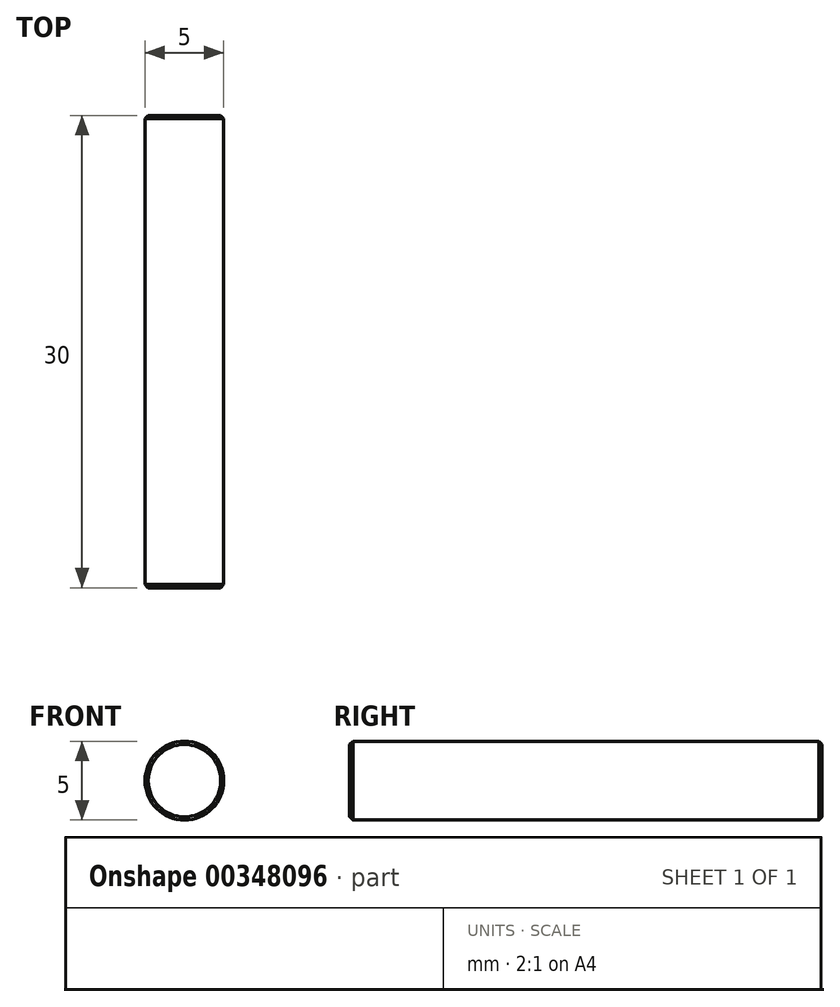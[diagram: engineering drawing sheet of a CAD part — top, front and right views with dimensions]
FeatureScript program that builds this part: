
annotation { "Feature Type Name" : "Feature", "Feature Type Description" : "" }
export const myFeature = defineFeature(function(context is Context, id is Id, definition is map)
    precondition{}
    {
        {
            var Q0;
            Q0=qCreatedBy(makeId("Front.planeOp"),FACE);
            var sketch = newSketch(context, id + "F0", { "sketchPlane" : qUnion([Q0])});
            skCircle(sketch, "E0", {"center": v(-60.1, 26.71) * mm, "radius": 2.5 * mm});
            skSolve(sketch);
        }
        {
            var Q0;
            Q0=makeQuery(id+"F0.imprint","IMPRINT",FACE,{"disambiguationData":[TD([[makeQuery(id+"F0.imprint","IMPRINT",EDGE,{"derivedFrom":sQuery(id+"F0.wireOp",EDGE,"E0")}),1.0]])]});
            extrude(context, id + "F1", {"entities" : qUnion([Q0]), "depth" : 30 * mm});
        }
        {
            var Q0;
            Q0=makeQuery(id+"F1.opExtrude","CAP_EDGE",EDGE,{"disambiguationData":[OSD([sQuery(id+"F0.wireOp",EDGE,"E0")])],"isStart":false});
            var Q1;
            Q1=makeQuery(id+"F1.opExtrude","CAP_FACE",FACE,{"disambiguationData":[OSD([sQuery(id+"F0.wireOp",EDGE,"E0")])],"isStart":true});
            chamfer(context, id + "F2", {"entities" : qUnion([Q0, Q1]), "width" : 0.2 * mm, "tangentPropagation" : true});
        }
    });
